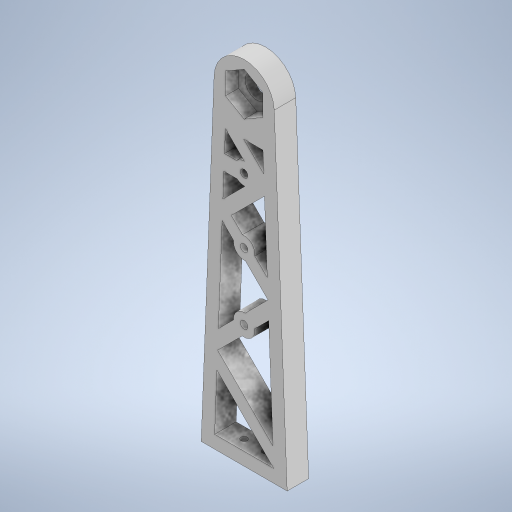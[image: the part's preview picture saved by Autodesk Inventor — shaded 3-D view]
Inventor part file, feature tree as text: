
AUTODESK INVENTOR PART (.ipt)
format: ipt  version: 2023 (Build 270158000, 158)  size: 475,648 bytes
history: native  units: mm
features: extrude x13, sketch x13, other x3, revolve x1, pattern_circular x1
ambient origin geometry x8: Origin, YZ Plane, XZ Plane, XY Plane, X Axis, Y Axis, Z Axis, Center Point
bodies: Body1 (feature_tree)
feature tree (31):
  other  "솔리드1"
  extrude  "돌출1"  Depth=66.0mm
  extrude  "돌출2"  Depth=10.0mm
  other  "작업 평면1"
  extrude  "돌출3"  Depth=10.0mm
  extrude  "돌출4"  Depth=30.0mm
  extrude  "돌출5"  Depth=50.0mm TaperAngle=0.0deg
  extrude  "돌출6"  Depth=28.0mm
  other  "작업 평면2"
  revolve  "회전1"
  extrude  "돌출7"  Depth=150.0mm
  extrude  "돌출8"  Depth=10.0mm TaperAngle=0.0deg
  pattern_circular  "원형 패턴1"  [2 undecoded]
  extrude  "돌출11"  Depth=6.0mm
  extrude  "돌출12"  Depth=6.0mm
  sketch  "스케치14"
  extrude  "돌출13"  Depth=10.0mm TaperAngle=0.0deg
  extrude  "돌출14"  Depth=6.0mm
  extrude  "돌출15"  TaperAngle=45.0deg  [1 undecoded]
  sketch  "스케치1"
  sketch  "스케치2"
  sketch  "스케치3"
  sketch  "스케치4"
  sketch  "스케치5"
  sketch  "스케치6"
  sketch  "스케치7"
  sketch  "스케치8"
  sketch  "스케치9"
  sketch  "스케치12"
  sketch  "스케치13"
  sketch  "스케치15"
note: 3 required parameter values undecoded (feature->parameter linkage not recoverable at this tier; creation-order binding heuristic only, values carry confidence <= 0.55)
